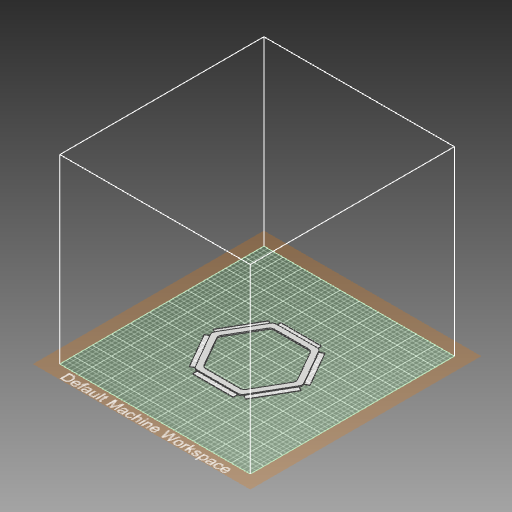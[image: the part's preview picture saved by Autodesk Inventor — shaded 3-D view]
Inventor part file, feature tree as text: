
AUTODESK INVENTOR PART (.ipt)
format: ipt  version: 2019 (Build 230136000, 136)  size: 480,256 bytes
history: native  units: mm
features: sketch x4, extrude x3, projected_geometry x3, fillet x2, other x1, pattern_circular x1, hole x1
ambient origin geometry x8: Origin, YZ Plane, XZ Plane, XY Plane, X Axis, Y Axis, Z Axis, Center Point
bodies: Solid1 (feature_tree)
feature tree (15):
  extrude  "Extrusion1"  Depth=2.0mm TaperAngle=0.0deg
  extrude  "Extrusion6"  Depth=10.0mm
  fillet  "Fillet2"  Radius=10.0mm
  fillet  "Fillet3"  Radius=12.0mm
  extrude  "Extrusion7"  Depth=0.5mm TaperAngle=0.0deg
  other  "Work Axis1"
  pattern_circular  "Circular Pattern1"  Count=6 Angle=360.0deg
  hole  "Hole1"  [1 undecoded]
  sketch  "Sketch1"  dims[d0=175.0mm d1=2.0mm d2=0.0mm]
  sketch  "Sketch7"  dims[d20=7.0mm d21=0.0mm d24=10.0mm d25=10.0mm d26=12.0mm]
  projected_geometry  "Projected Loop7"
  sketch  "Sketch8"  dims[d27=10.0mm d28=0.5mm d29=0.0mm d30=60.0mm d31=360.0deg]
  projected_geometry  "Projected Loop8"
  sketch  "Sketch9"  dims[d33=60.0mm d35=360.0deg d37=3.0mm d38=6.0mm d39=10.0mm d40=2.0mm d41=90.0deg d42=26.75mm d43=0.0mm]
  projected_geometry  "Projected Loop9"
note: 1 required parameter value undecoded (feature->parameter linkage not recoverable at this tier; creation-order binding heuristic only, values carry confidence <= 0.55)
